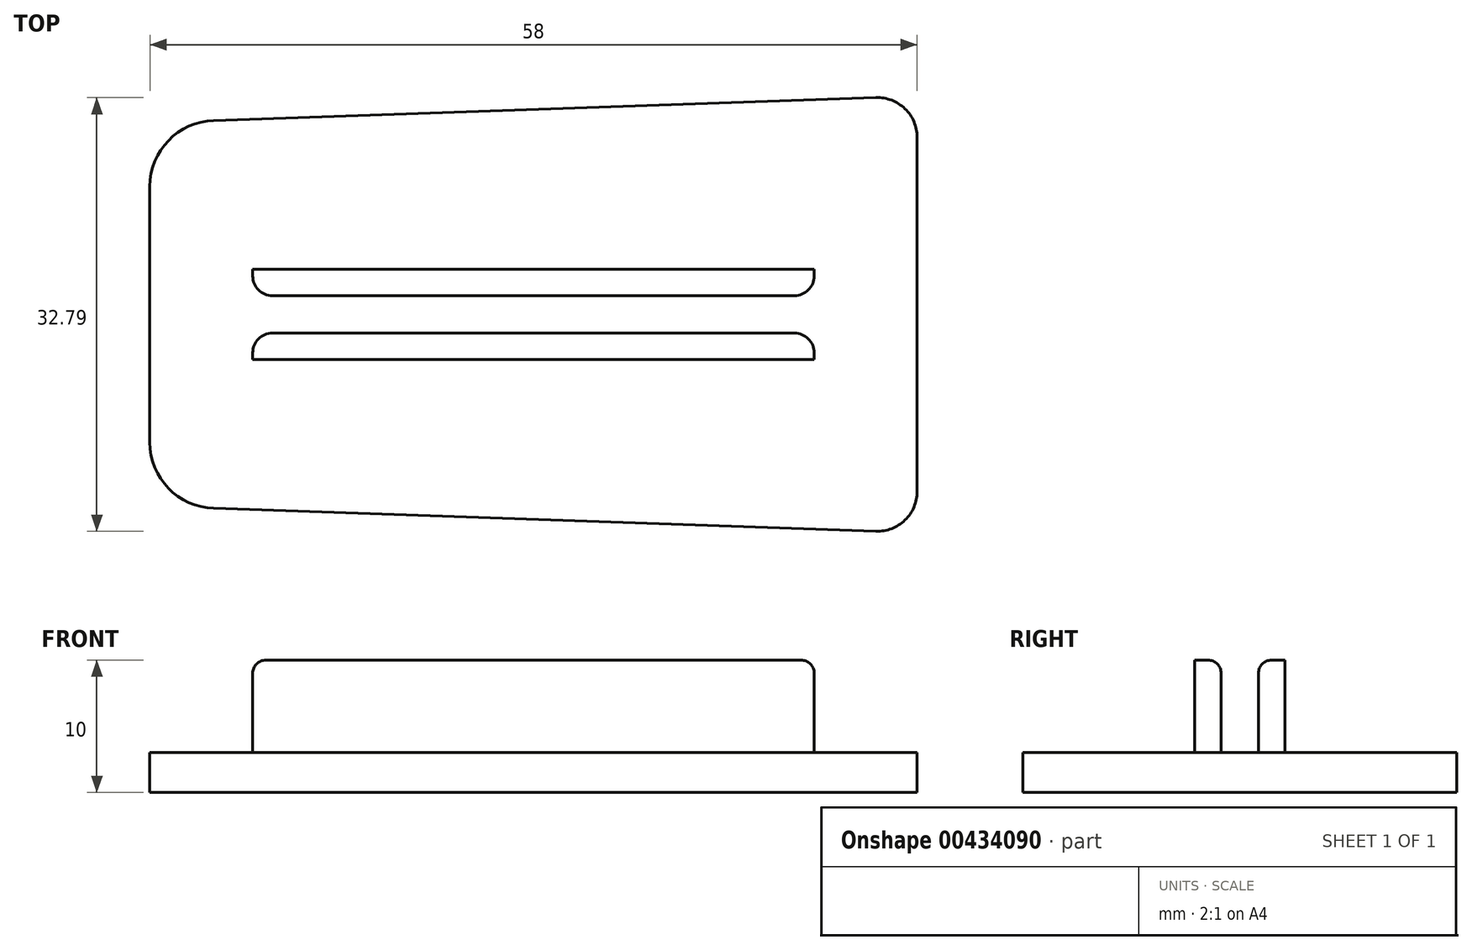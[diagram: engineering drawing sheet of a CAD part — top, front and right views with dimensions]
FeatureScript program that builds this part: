
annotation { "Feature Type Name" : "Feature", "Feature Type Description" : "" }
export const myFeature = defineFeature(function(context is Context, id is Id, definition is map)
    precondition{}
    {
        {
            var Q0;
            Q0=qCreatedBy(makeId("Top.planeOp"),FACE);
            var sketch = newSketch(context, id + "F0", { "sketchPlane" : qUnion([Q0])});
            skLineSegment(sketch, "E0.left", {"start": v(-65.71, 36.47) * mm, "end": v(-65.71, 33.65) * mm});
            skLineSegment(sketch, "E0.right", {"start": v(-7.71, 51.56) * mm, "end": v(-7.71, 18.56) * mm});
            skLineSegment(sketch, "E1", {"start": v(-81.04, 35.06) * mm, "end": v(-57.94, 35.06) * mm, "construction": true});
            skPoint(sketch, "E1.startSnap0", {"position": v(-65.71, 35.06) * mm});
            skLineSegment(sketch, "E2", {"start": v(-36.71, 62.88) * mm, "end": v(-36.71, 8.4) * mm, "construction": true});
            skPoint(sketch, "E2.startSnap0", {"position": v(-36.71, 51.56) * mm});
            skLineSegment(sketch, "E3.0", {"start": v(-57.94, 33.65) * mm, "end": v(-15.49, 33.65) * mm, "construction": true});
            skLineSegment(sketch, "E4.0", {"start": v(-57.94, 36.47) * mm, "end": v(-15.49, 36.47) * mm, "construction": true});
            skLineSegment(sketch, "E5", {"start": v(-57.94, 38.47) * mm, "end": v(-57.94, 36.47) * mm, "construction": true});
            skLineSegment(sketch, "E6.MirrorCS", {"start": v(-15.49, 38.47) * mm, "end": v(-15.49, 36.47) * mm, "construction": true});
            skLineSegment(sketch, "E7.top", {"start": v(-57.94, 38.47) * mm, "end": v(-15.49, 38.47) * mm, "construction": true});
            skLineSegment(sketch, "E7.left", {"start": v(-57.94, 36.47) * mm, "end": v(-57.94, 38.47) * mm, "construction": true});
            skLineSegment(sketch, "E7.right", {"start": v(-15.49, 36.47) * mm, "end": v(-15.49, 38.47) * mm, "construction": true});
            skLineSegment(sketch, "E8.top", {"start": v(-57.94, 33.65) * mm, "end": v(-15.49, 33.65) * mm});
            skLineSegment(sketch, "E9.bottom", {"start": v(-57.94, 38.47) * mm, "end": v(-15.49, 38.47) * mm});
            skLineSegment(sketch, "E9.top", {"start": v(-57.94, 36.47) * mm, "end": v(-15.49, 36.47) * mm});
            skLineSegment(sketch, "E9.left", {"start": v(-57.94, 38.47) * mm, "end": v(-57.94, 36.47) * mm});
            skLineSegment(sketch, "E9.right", {"start": v(-15.49, 38.47) * mm, "end": v(-15.49, 36.47) * mm});
            skLineSegment(sketch, "E10.trimOffspring", {"start": v(-15.49, 35.06) * mm, "end": v(7.2, 35.06) * mm, "construction": true});
            skLineSegment(sketch, "E11.trimOffspring", {"start": v(-57.94, 33.65) * mm, "end": v(-57.94, 31.65) * mm, "construction": true});
            skLineSegment(sketch, "E12.top", {"start": v(-57.94, 31.65) * mm, "end": v(-15.49, 31.65) * mm});
            skLineSegment(sketch, "E12.left", {"start": v(-57.94, 33.65) * mm, "end": v(-57.94, 31.65) * mm});
            skLineSegment(sketch, "E12.right", {"start": v(-15.49, 33.65) * mm, "end": v(-15.49, 31.65) * mm});
            skLineSegment(sketch, "E13", {"start": v(-57.94, 35.06) * mm, "end": v(-15.49, 35.06) * mm, "construction": true});
            skLineSegment(sketch, "E14", {"start": v(-65.71, 35.06) * mm, "end": v(-65.71, 49.56) * mm});
            skLineSegment(sketch, "E15", {"start": v(-65.71, 49.56) * mm, "end": v(-7.71, 51.56) * mm});
            skLineSegment(sketch, "E16.MirrorCS", {"start": v(-65.71, 20.56) * mm, "end": v(-7.71, 18.56) * mm});
            skPoint(sketch, "E0.bottom.start.orphan", {"position": v(-65.71, 51.56) * mm});
            skPoint(sketch, "E17.orphan", {"position": v(-65.71, 18.56) * mm});
            skLineSegment(sketch, "E18", {"start": v(-65.71, 35.06) * mm, "end": v(-65.71, 18.56) * mm});
            skPoint(sketch, "E19.orphan", {"position": v(-57.94, 26.23) * mm});
            skPoint(sketch, "E20.orphan", {"position": v(-57.94, 42.1) * mm});
            skPoint(sketch, "E21.orphan", {"position": v(-15.49, 42.1) * mm});
            skPoint(sketch, "E22.orphan", {"position": v(-15.49, 26.23) * mm});
            skLineSegment(sketch, "E23.trimOffspring", {"start": v(-15.49, 33.65) * mm, "end": v(-15.49, 31.65) * mm, "construction": true});
            skSolve(sketch);
        }
        {
            var Q0;
            Q0=makeQuery(id+"F0.imprint","IMPRINT",FACE,{"disambiguationData":[TD([[makeQuery(id+"F0.imprint","IMPRINT",EDGE,{"derivedFrom":sQuery(id+"F0.wireOp",EDGE,"E0.right")}),-1.0]])]});
            extrude(context, id + "F1", {"entities" : qUnion([Q0]), "depth" : 3 * mm, "offsetDistance" : 25 * mm});
        }
        {
            var Q0;
            Q0=makeQuery(id+"F0.imprint","IMPRINT",FACE,{"disambiguationData":[TD([[makeQuery(id+"F0.imprint","IMPRINT",EDGE,{"derivedFrom":sQuery(id+"F0.wireOp",EDGE,"E8.top")}),-1.0]])]});
            var Q1;
            Q1=makeQuery(id+"F0.imprint","IMPRINT",FACE,{"disambiguationData":[TD([[makeQuery(id+"F0.imprint","IMPRINT",EDGE,{"derivedFrom":sQuery(id+"F0.wireOp",EDGE,"E9.bottom")}),-1.0]])]});
            extrude(context, id + "F2", {"entities" : qUnion([Q0, Q1]), "operationType" : NewBodyOperationType.ADD, "depth" : 10 * mm, "offsetDistance" : 25 * mm});
        }
        {
            var Q0;
            Q0=makeQuery(id+"F2.opExtrude","SWEPT_EDGE",EDGE,{"disambiguationData":[OSD([sQuery(id+"F0.wireOp",EDGE,"E9.top"),sQuery(id+"F0.wireOp",EDGE,"E9.left")])]});
            var Q1;
            Q1=makeQuery(id+"F2.opExtrude","SWEPT_EDGE",EDGE,{"disambiguationData":[OSD([sQuery(id+"F0.wireOp",EDGE,"E8.top"),sQuery(id+"F0.wireOp",EDGE,"E12.left")])]});
            var Q2;
            Q2=makeQuery(id+"F2.opExtrude","SWEPT_EDGE",EDGE,{"disambiguationData":[OSD([sQuery(id+"F0.wireOp",EDGE,"E9.top"),sQuery(id+"F0.wireOp",EDGE,"E9.right")])]});
            var Q3;
            Q3=makeQuery(id+"F2.opExtrude","SWEPT_EDGE",EDGE,{"disambiguationData":[OSD([sQuery(id+"F0.wireOp",EDGE,"E8.top"),sQuery(id+"F0.wireOp",EDGE,"E12.right")])]});
            fillet(context, id + "F3", {"entities" : qUnion([Q0, Q1, Q2, Q3]), "radius" : 1.5 * mm, "tangentPropagation" : true, "allowEdgeOverflow" : false});
        }
        {
            var Q0;
            Q0=makeQuery(id+"F2.opExtrude","CAP_EDGE",EDGE,{"disambiguationData":[OSD([sQuery(id+"F0.wireOp",EDGE,"E9.top")])],"isStart":false});
            var Q1;
            Q1=makeQuery(id+"F2.opExtrude","CAP_EDGE",EDGE,{"disambiguationData":[OSD([sQuery(id+"F0.wireOp",EDGE,"E8.top")])],"isStart":false});
            fillet(context, id + "F4", {"entities" : qUnion([Q0, Q1]), "radius" : 1 * mm, "tangentPropagation" : true, "allowEdgeOverflow" : false});
        }
        {
            var Q0;
            Q0=makeQuery(id+"F1.opExtrude","SWEPT_EDGE",EDGE,{"disambiguationData":[OSD([sQuery(id+"F0.wireOp",EDGE,"E0.bottom"),sQuery(id+"F0.wireOp",EDGE,"E0.right")])]});
            var Q1;
            Q1=makeQuery(id+"F1.opExtrude","SWEPT_EDGE",EDGE,{"disambiguationData":[OSD([sQuery(id+"F0.wireOp",EDGE,"E0.top"),sQuery(id+"F0.wireOp",EDGE,"E0.left")])]});
            var Q2;
            Q2=makeQuery(id+"F1.opExtrude","SWEPT_EDGE",EDGE,{"disambiguationData":[OSD([sQuery(id+"F0.wireOp",EDGE,"E0.bottom"),sQuery(id+"F0.wireOp",EDGE,"E0.left")])]});
            var Q3;
            Q3=makeQuery(id+"F1.opExtrude","SWEPT_EDGE",EDGE,{"disambiguationData":[OSD([sQuery(id+"F0.wireOp",EDGE,"E0.top"),sQuery(id+"F0.wireOp",EDGE,"E0.right")])]});
            fillet(context, id + "F5", {"entities" : qUnion([Q0, Q1, Q2, Q3]), "radius" : 3 * mm, "tangentPropagation" : true, "allowEdgeOverflow" : false});
        }
        {
            var Q0;
            Q0=makeQuery(id+"F1.opExtrude","SWEPT_EDGE",EDGE,{"disambiguationData":[OSD([sQuery(id+"F0.wireOp",EDGE,"E16.MirrorCS"),sQuery(id+"F0.wireOp",EDGE,"E18")])]});
            var Q1;
            Q1=makeQuery(id+"F1.opExtrude","SWEPT_EDGE",EDGE,{"disambiguationData":[OSD([sQuery(id+"F0.wireOp",EDGE,"E14"),sQuery(id+"F0.wireOp",EDGE,"E15")])]});
            fillet(context, id + "F6", {"entities" : qUnion([Q0, Q1]), "radius" : 5 * mm, "tangentPropagation" : true, "allowEdgeOverflow" : false});
        }
    });
